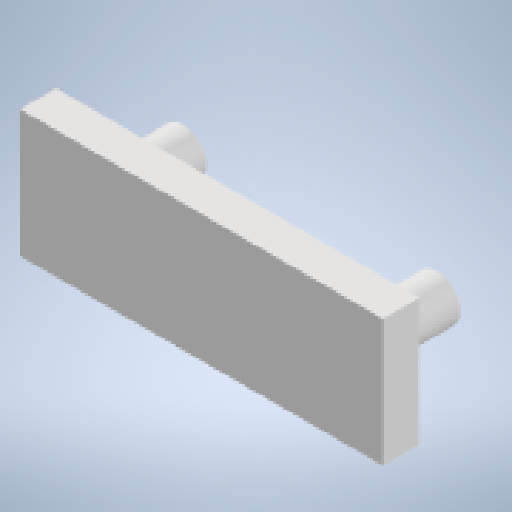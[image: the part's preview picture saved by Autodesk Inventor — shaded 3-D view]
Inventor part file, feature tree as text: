
AUTODESK INVENTOR PART (.ipt)
format: ipt  version: 2023 (Build 270158000, 158)  size: 124,416 bytes
history: native  units: mm
features: extrude x2, sketch x1, reference x1, other x1
ambient origin geometry x8: Origin, YZ Plane, XZ Plane, XY Plane, X Axis, Y Axis, Z Axis, Center Point
bodies: Solid1 (feature_tree)
feature tree (5):
  sketch  "Sketch2"  dims[d0=2.0mm d1=0.0mm d2=4.0mm d3=0.0mm]
  extrude  "Extrusion1"  Depth=4.0mm TaperAngle=0.0deg
  extrude  "Extrusion2"  [1 undecoded]
  reference  "Reference1"
  other  "3D_skenner.iam"
note: 1 required parameter value undecoded (feature->parameter linkage not recoverable at this tier; creation-order binding heuristic only, values carry confidence <= 0.55)
